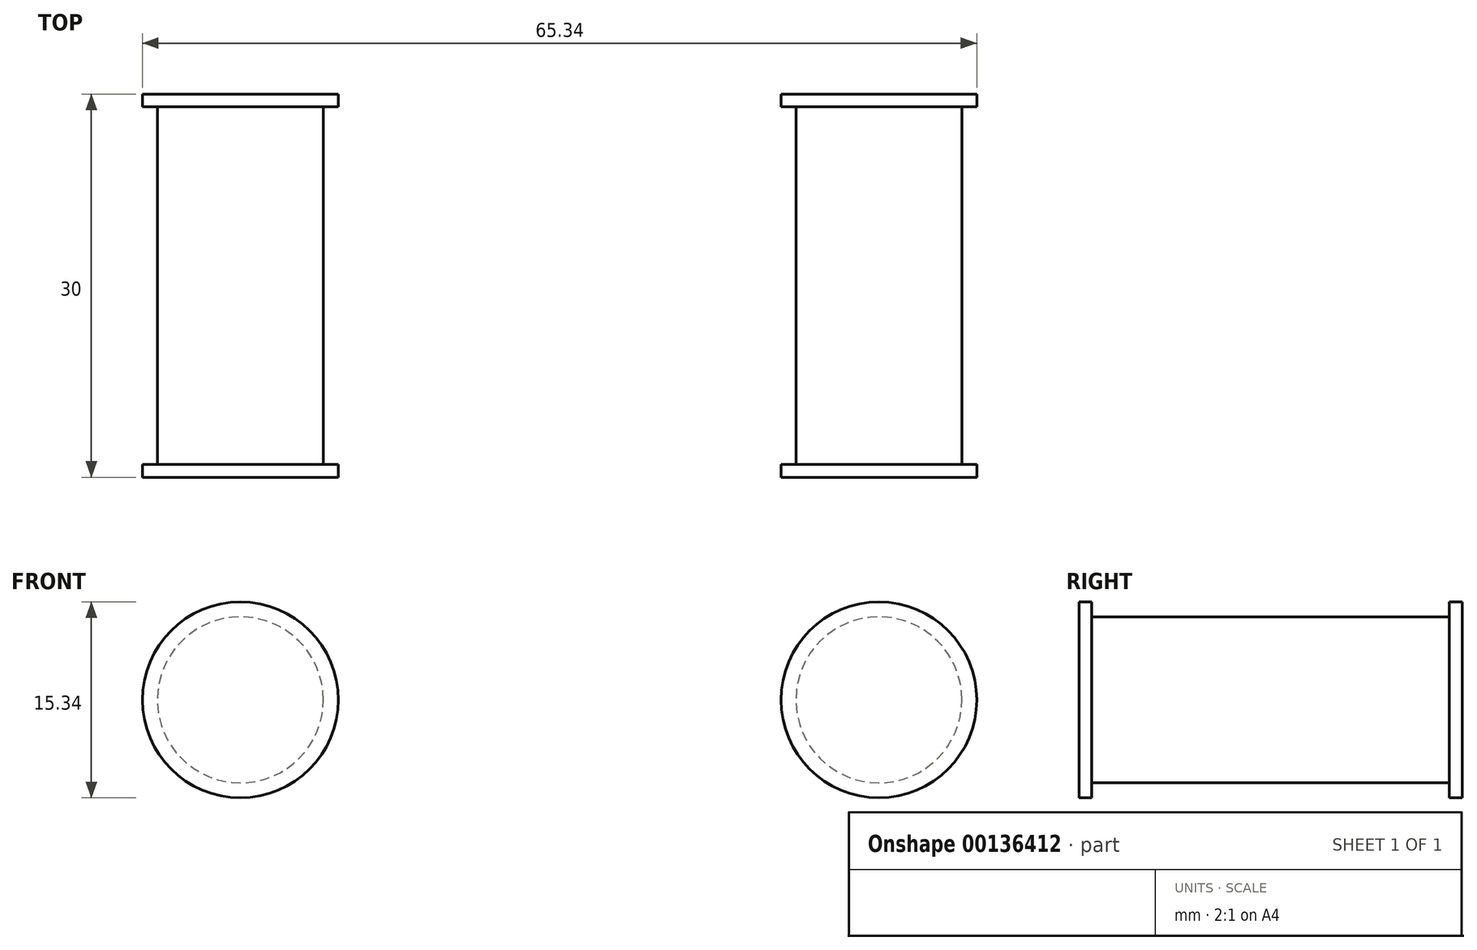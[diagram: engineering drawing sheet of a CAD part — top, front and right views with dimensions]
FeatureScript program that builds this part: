
annotation { "Feature Type Name" : "Feature", "Feature Type Description" : "" }
export const myFeature = defineFeature(function(context is Context, id is Id, definition is map)
    precondition{}
    {
        {
            var Q0;
            Q0=qCreatedBy(makeId("Front.planeOp"),FACE);
            var sketch = newSketch(context, id + "F0", { "sketchPlane" : qUnion([Q0])});
            skCircle(sketch, "E0", {"center": v(0, 0) * mm, "radius": 6.5 * mm});
            skSolve(sketch);
        }
        {
            var Q0;
            Q0 = qSketchRegion(id + "F0", true);
            extrude(context, id + "F1", {"entities" : qUnion([Q0]), "depth" : 28 * mm});
        }
        {
            var Q0;
            Q0=makeQuery(id+"F1.opExtrude","CAP_FACE",FACE,{"disambiguationData":[OSD([sQuery(id+"F0.wireOp",EDGE,"E0")])],"isStart":false});
            var sketch = newSketch(context, id + "F2", { "sketchPlane" : qUnion([Q0])});
            skCircle(sketch, "E1", {"center": v(0, 0) * mm, "radius": 7.67 * mm});
            skSolve(sketch);
        }
        {
            var Q0;
            Q0=makeQuery(id+"F1.opExtrude","CAP_FACE",FACE,{"disambiguationData":[OSD([sQuery(id+"F0.wireOp",EDGE,"E0")])],"isStart":true});
            var sketch = newSketch(context, id + "F3", { "sketchPlane" : qUnion([Q0])});
            skCircle(sketch, "E2", {"center": v(0, 0) * mm, "radius": 7.67 * mm});
            skSolve(sketch);
        }
        {
            var Q0;
            Q0 = qSketchRegion(id + "F2", true);
            extrude(context, id + "F4", {"entities" : qUnion([Q0]), "operationType" : NewBodyOperationType.ADD, "depth" : 1 * mm});
        }
        {
            var Q0;
            Q0 = qSketchRegion(id + "F3", true);
            extrude(context, id + "F5", {"entities" : qUnion([Q0]), "operationType" : NewBodyOperationType.ADD, "depth" : 1 * mm});
        }
        {
            var Q0;
            Q0=qCreatedBy(makeId("Right.planeOp"),FACE);
            cPlane(context, id + "F6", {"entities" : qUnion([Q0]), "cplaneType" : CPlaneType.OFFSET, "offset" : 25 * mm, "width" : 150 * mm, "height" : 150 * mm});
        }
        {
            var Q0;
            Q0=makeQuery(id+"F1.opExtrude","SWEPT_BODY",BODY,{"disambiguationData":[OSD([sQuery(id+"F0.wireOp",EDGE,"E0")])]});
            var Q1;
            Q1=qCreatedBy(id+"F6.planeOp",FACE);
            mirror(context, id + "F7", {"entities" : qUnion([Q0]), "mirrorPlane" : qUnion([Q1])});
        }
    });
